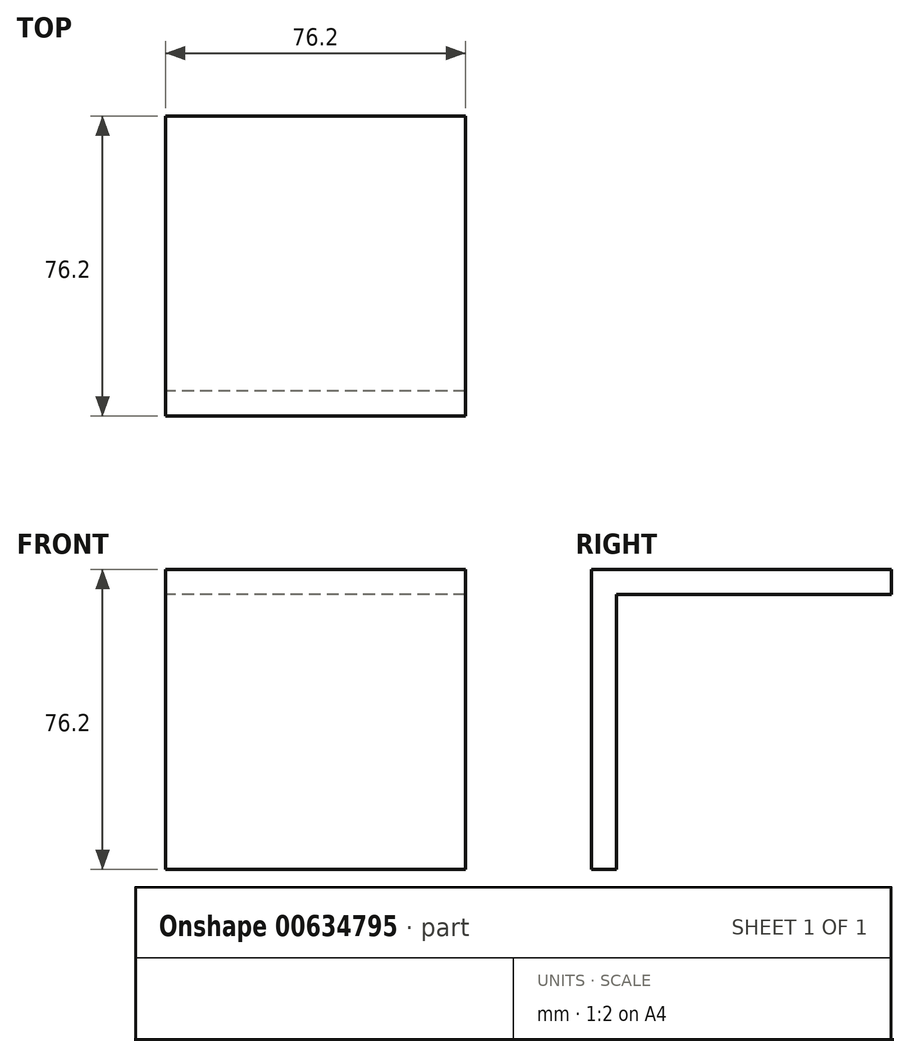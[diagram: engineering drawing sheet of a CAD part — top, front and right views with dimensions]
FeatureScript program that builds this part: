
annotation { "Feature Type Name" : "Feature", "Feature Type Description" : "" }
export const myFeature = defineFeature(function(context is Context, id is Id, definition is map)
    precondition{}
    {
        {
            var Q0;
            Q0=qCreatedBy(makeId("Right.planeOp"),FACE);
            var sketch = newSketch(context, id + "F0", { "sketchPlane" : qUnion([Q0])});
            skLineSegment(sketch, "E0", {"start": v(0, 0) * mm, "end": v(76.2, 0) * mm});
            skLineSegment(sketch, "E1", {"start": v(76.2, 0) * mm, "end": v(76.2, -6.35) * mm});
            skLineSegment(sketch, "E2", {"start": v(76.2, -6.35) * mm, "end": v(6.35, -6.35) * mm});
            skLineSegment(sketch, "E3", {"start": v(6.35, -6.35) * mm, "end": v(6.35, -76.2) * mm});
            skLineSegment(sketch, "E4", {"start": v(6.35, -76.2) * mm, "end": v(0, -76.2) * mm});
            skLineSegment(sketch, "E5", {"start": v(0, -76.2) * mm, "end": v(0, 0) * mm});
            skSolve(sketch);
        }
        {
            var Q0;
            Q0=makeQuery(id+"F0.imprint","IMPRINT",FACE,{"disambiguationData":[TD([[makeQuery(id+"F0.imprint","IMPRINT",EDGE,{"derivedFrom":sQuery(id+"F0.wireOp",EDGE,"E0")}),-1.0]])]});
            extrude(context, id + "F1", {"entities" : qUnion([Q0]), "endBound" : BoundingType.SYMMETRIC, "depth" : 76.2 * mm, "offsetDistance" : 25.4 * mm});
        }
    });
